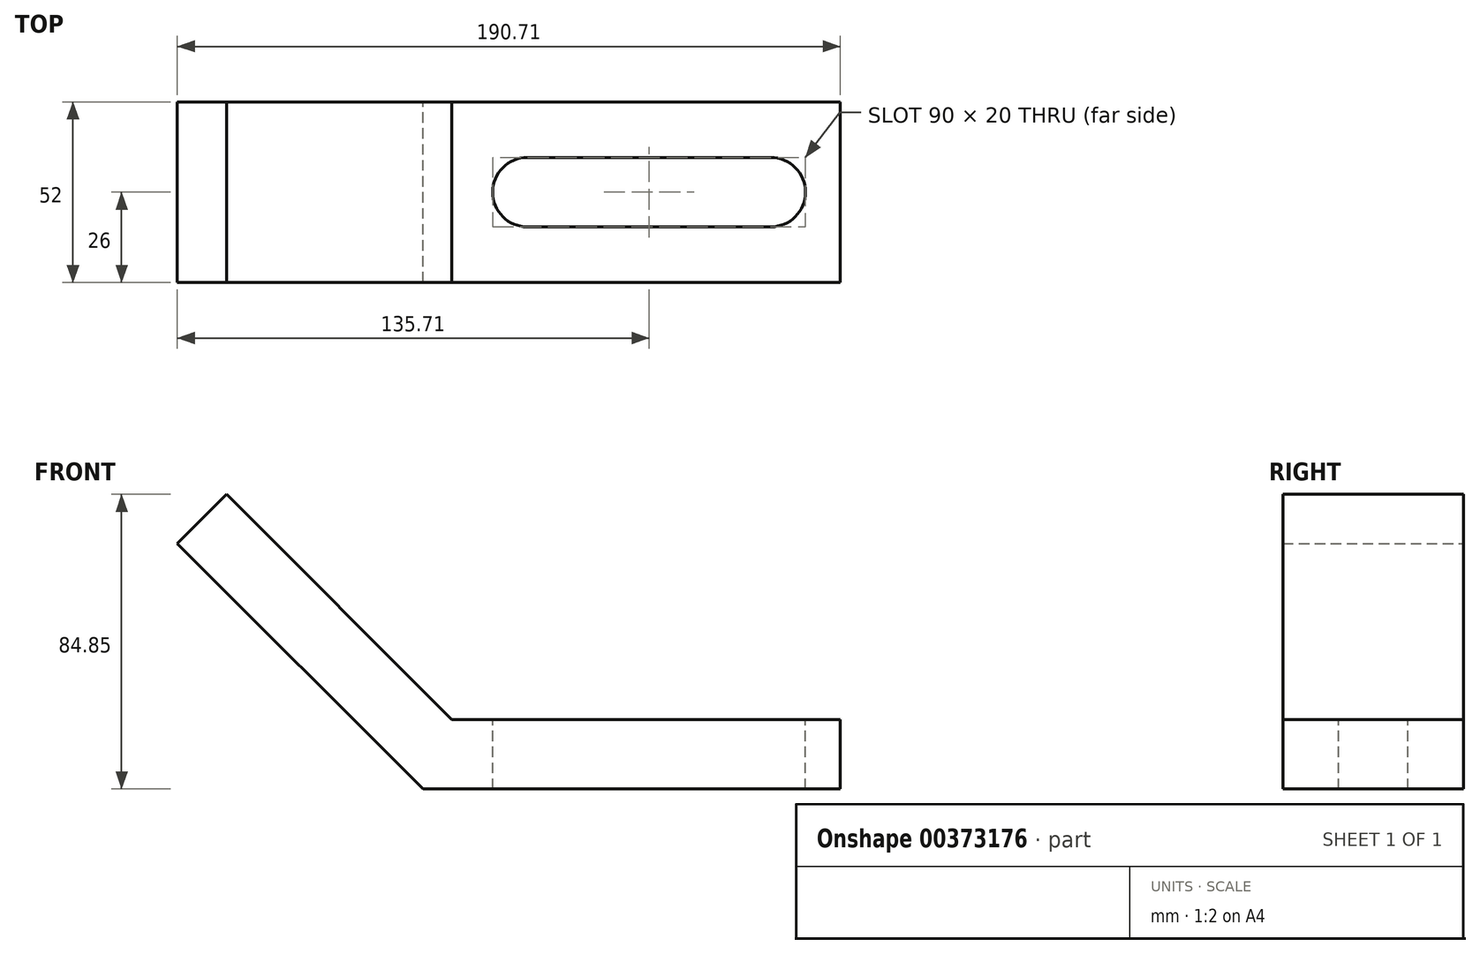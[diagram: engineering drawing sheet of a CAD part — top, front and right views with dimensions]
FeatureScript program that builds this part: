
annotation { "Feature Type Name" : "Feature", "Feature Type Description" : "" }
export const myFeature = defineFeature(function(context is Context, id is Id, definition is map)
    precondition{}
    {
        {
            var Q0;
            Q0=qCreatedBy(makeId("Front.planeOp"),FACE);
            var sketch = newSketch(context, id + "F0", { "sketchPlane" : qUnion([Q0])});
            skLineSegment(sketch, "E0", {"start": v(0, 0) * mm, "end": v(120, 0) * mm});
            skLineSegment(sketch, "E1", {"start": v(0, 0) * mm, "end": v(-70.71, 70.71) * mm});
            skLineSegment(sketch, "E2.0", {"start": v(8.28, 20) * mm, "end": v(-56.57, 84.85) * mm});
            skLineSegment(sketch, "E2.1", {"start": v(8.28, 20) * mm, "end": v(120, 20) * mm});
            skLineSegment(sketch, "E3", {"start": v(-56.57, 84.85) * mm, "end": v(-70.71, 70.71) * mm});
            skLineSegment(sketch, "E4", {"start": v(120, 20) * mm, "end": v(120, 0) * mm});
            skSolve(sketch);
        }
        {
            var Q0;
            Q0 = qSketchRegion(id + "F0", true);
            extrude(context, id + "F1", {"entities" : qUnion([Q0]), "depth" : 52 * mm, "symmetric" : true});
        }
        {
            var Q0;
            Q0=makeQuery(id+"F1.opExtrude","SWEPT_FACE",FACE,{"disambiguationData":[OSD([sQuery(id+"F0.wireOp",EDGE,"E2.1")])]});
            var sketch = newSketch(context, id + "F2", { "sketchPlane" : qUnion([Q0])});
            skLineSegment(sketch, "E5", {"start": v(8.28, 0) * mm, "end": v(13.4, 0) * mm, "construction": true});
            skPoint(sketch, "E5.endSnap0", {"position": v(8.28, 0) * mm});
            skLineSegment(sketch, "E6", {"start": v(120, 0) * mm, "end": v(8.28, 0) * mm, "construction": true});
            skArc(sketch, "E7", {"start": v(100, -10) * mm, "mid": v(110, 0) * mm, "end": v(100, 10) * mm});
            skArc(sketch, "E8", {"start": v(30, 10) * mm, "mid": v(20, 0) * mm, "end": v(30, -10) * mm});
            skLineSegment(sketch, "E9", {"start": v(30, 10) * mm, "end": v(100, 10) * mm});
            skLineSegment(sketch, "E10", {"start": v(30, -10) * mm, "end": v(100, -10) * mm});
            skSolve(sketch);
        }
        {
            var Q0;
            Q0 = qSketchRegion(id + "F2", true);
            extrude(context, id + "F3", {"entities" : qUnion([Q0]), "operationType" : NewBodyOperationType.REMOVE, "endBound" : BoundingType.THROUGH_ALL, "oppositeDirection" : true, "depth" : 25.4 * mm});
        }
        {
            var Q0;
            Q0=makeQuery(id+"F1.opExtrude","SWEPT_FACE",FACE,{"disambiguationData":[OSD([sQuery(id+"F0.wireOp",EDGE,"E2.0")])]});
            var sketch = newSketch(context, id + "F4", { "sketchPlane" : qUnion([Q0])});
            skPoint(sketch, "E11.centerSnap0", {"position": v(-100, 0) * mm});
            skCircle(sketch, "E12", {"center": v(-74, 0) * mm, "radius": 10 * mm});
            skArc(sketch, "E13", {"start": v(-74, 26) * mm, "mid": v(-100, 0) * mm, "end": v(-74, -26) * mm});
            skLineSegment(sketch, "E14", {"start": v(-74, 26) * mm, "end": v(-100, 26) * mm});
            skLineSegment(sketch, "E15", {"start": v(-100, 26) * mm, "end": v(-100, -26) * mm});
            skLineSegment(sketch, "E16", {"start": v(-100, -26) * mm, "end": v(-74, -26) * mm});
            skSolve(sketch);
        }
        {
            var Q0;
            Q0 = qSketchRegion(id + "F4", true);
            extrude(context, id + "F5", {"entities" : qUnion([Q0]), "operationType" : NewBodyOperationType.REMOVE, "endBound" : BoundingType.THROUGH_ALL, "oppositeDirection" : true, "depth" : 25.4 * mm});
        }
    });
